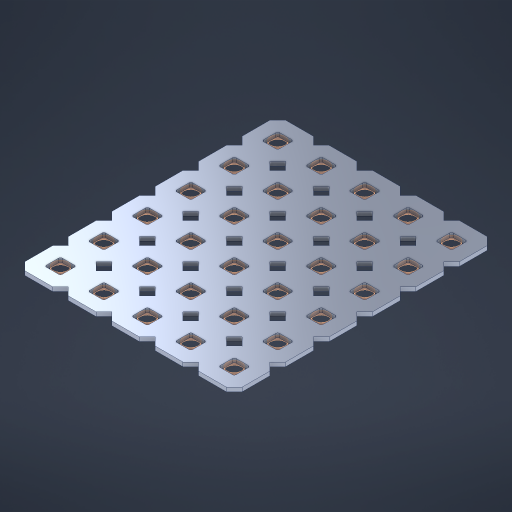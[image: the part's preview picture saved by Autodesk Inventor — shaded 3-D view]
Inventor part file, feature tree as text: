
AUTODESK INVENTOR PART (.ipt)
format: ipt  version: 2023 (Build 270158000, 158)  size: 614,912 bytes
history: native  units: in
note: dims shown in document units (in); Inventor stores cm internally (conversion verified against a paired STEP export)
features: other x31, extrude x29, sketch x2, pattern_linear x1
ambient origin geometry x8: Origin, YZ Plane, XZ Plane, XY Plane, X Axis, Y Axis, Z Axis, Center Point
bodies: Solid1 (feature_tree), Body (feature_tree)
feature tree (63):
  pattern_linear  "Rectangular Pattern1"  Spacing1=0.09in  [1 undecoded]
  sketch  "Sketch1"  dims[d1=0.5in]
  sketch  "Sketch2"  dims[d2=0.182in d3=0.09in d4=0.09in d5=0.09in d6=0.09in d7=0.09in d8=0.09in d9=0.09in d10=0.09in d11=0.02in d13=0.0in d14=0.172in d15=0.0625in d16=0.0in d19=0.5in d22=0.5in]
  other  "Srf1"
  other  "Srf126"
  other  "Srf127"
  other  "Srf128"
  other  "Srf129"
  other  "Srf130"
  other  "Srf268"
  other  "Srf269"
  other  "Srf270"
  other  "Srf271"
  other  "Srf272"
  other  "Srf273"
  other  "Srf293"
  other  "Srf294"
  other  "Srf295"
  other  "Srf296"
  other  "Srf297"
  other  "Srf298"
  other  "Srf318"
  other  "Srf319"
  other  "Srf320"
  other  "Srf321"
  other  "Srf322"
  other  "Srf323"
  other  "Srf343"
  other  "Srf344"
  other  "Srf345"
  other  "Srf346"
  other  "Srf347"
  other  "Srf348"
  other  "Circle"
  extrude  "ExtrusionSrf126"  Depth=0.09in
  extrude  "ExtrusionSrf127"  Depth=0.09in
  extrude  "ExtrusionSrf128"  Depth=0.09in
  extrude  "ExtrusionSrf129"  Depth=0.09in
  extrude  "ExtrusionSrf130"  Depth=0.09in
  extrude  "ExtrusionSrf268"  Depth=0.09in
  extrude  "ExtrusionSrf269"  Depth=0.09in
  extrude  "ExtrusionSrf270"  Depth=0.02in
  extrude  "ExtrusionSrf271"  TaperAngle=0.0deg  [1 undecoded]
  extrude  "ExtrusionSrf272"  Depth=0.5in
  extrude  "ExtrusionSrf273"  Depth=0.5in TaperAngle=0.0deg
  extrude  "ExtrusionSrf293"  Depth=0.5in
  extrude  "ExtrusionSrf294"  Depth=0.5in
  extrude  "ExtrusionSrf295"  [1 undecoded]
  extrude  "ExtrusionSrf296"  [1 undecoded]
  extrude  "ExtrusionSrf297"  [1 undecoded]
  extrude  "ExtrusionSrf298"  [1 undecoded]
  extrude  "ExtrusionSrf318"  [1 undecoded]
  extrude  "ExtrusionSrf319"  [1 undecoded]
  extrude  "ExtrusionSrf320"  [1 undecoded]
  extrude  "ExtrusionSrf321"  [1 undecoded]
  extrude  "ExtrusionSrf322"  [1 undecoded]
  extrude  "ExtrusionSrf323"  [1 undecoded]
  extrude  "ExtrusionSrf343"  [1 undecoded]
  extrude  "ExtrusionSrf344"  [1 undecoded]
  extrude  "ExtrusionSrf345"  [1 undecoded]
  extrude  "ExtrusionSrf346"  [1 undecoded]
  extrude  "ExtrusionSrf347"  [1 undecoded]
  extrude  "ExtrusionSrf348"  [1 undecoded]
note: 18 required parameter values undecoded (feature->parameter linkage not recoverable at this tier; creation-order binding heuristic only, values carry confidence <= 0.55)
